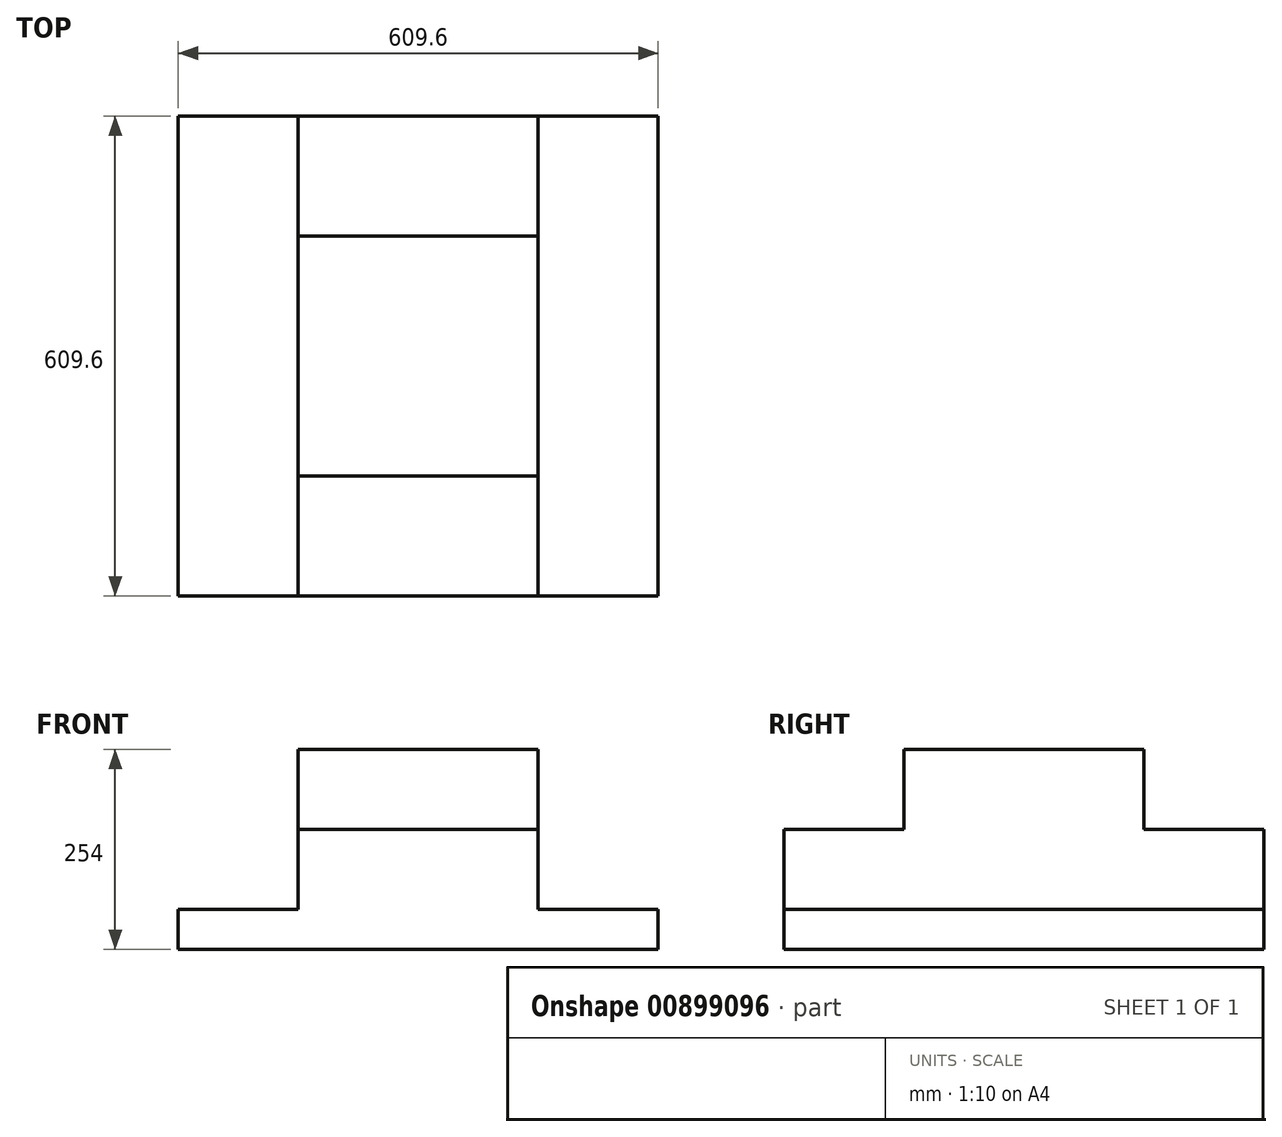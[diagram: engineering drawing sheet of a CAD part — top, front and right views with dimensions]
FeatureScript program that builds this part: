
annotation { "Feature Type Name" : "Feature", "Feature Type Description" : "" }
export const myFeature = defineFeature(function(context is Context, id is Id, definition is map)
    precondition{}
    {
        {
            var Q0;
            Q0=qCreatedBy(makeId("Top.planeOp"),FACE);
            var sketch = newSketch(context, id + "F0", { "sketchPlane" : qUnion([Q0])});
            skLineSegment(sketch, "E0.bottom", {"start": v(-152.4, 304.8) * mm, "end": v(152.4, 304.8) * mm});
            skLineSegment(sketch, "E0.top", {"start": v(-152.4, -304.8) * mm, "end": v(152.4, -304.8) * mm});
            skLineSegment(sketch, "E0.left", {"start": v(-152.4, 304.8) * mm, "end": v(-152.4, -304.8) * mm});
            skLineSegment(sketch, "E0.right", {"start": v(152.4, 304.8) * mm, "end": v(152.4, -304.8) * mm});
            skSolve(sketch);
        }
        {
            var Q0;
            Q0=makeQuery(id+"F0.imprint","IMPRINT",FACE,{"disambiguationData":[TD([[makeQuery(id+"F0.imprint","IMPRINT",EDGE,{"derivedFrom":sQuery(id+"F0.wireOp",EDGE,"E0.bottom")}),-1.0]])]});
            extrude(context, id + "F1", {"entities" : qUnion([Q0]), "depth" : 101.6 * mm, "offsetDistance" : 25.4 * mm});
        }
        {
            var Q0;
            Q0=qCreatedBy(makeId("Top.planeOp"),FACE);
            var sketch = newSketch(context, id + "F2", { "sketchPlane" : qUnion([Q0])});
            skLineSegment(sketch, "E1.bottom", {"start": v(-304.8, 304.8) * mm, "end": v(304.8, 304.8) * mm});
            skLineSegment(sketch, "E1.top", {"start": v(-304.8, -304.8) * mm, "end": v(304.8, -304.8) * mm});
            skLineSegment(sketch, "E1.left", {"start": v(-304.8, 304.8) * mm, "end": v(-304.8, -304.8) * mm});
            skLineSegment(sketch, "E1.right", {"start": v(304.8, 304.8) * mm, "end": v(304.8, -304.8) * mm});
            skSolve(sketch);
        }
        {
            var Q0;
            Q0=makeQuery(id+"F2.imprint","IMPRINT",FACE,{"disambiguationData":[TD([[makeQuery(id+"F2.imprint","IMPRINT",EDGE,{"derivedFrom":sQuery(id+"F2.wireOp",EDGE,"E1.bottom")}),-1.0]])]});
            extrude(context, id + "F3", {"entities" : qUnion([Q0]), "operationType" : NewBodyOperationType.ADD, "oppositeDirection" : true, "depth" : 50.8 * mm, "offsetDistance" : 25.4 * mm});
        }
        {
            var Q0;
            Q0=makeQuery(id+"F1.opExtrude","CAP_FACE",FACE,{"disambiguationData":[OSD([sQuery(id+"F0.wireOp",EDGE,"E0.bottom"),sQuery(id+"F0.wireOp",EDGE,"E0.top"),sQuery(id+"F0.wireOp",EDGE,"E0.left"),sQuery(id+"F0.wireOp",EDGE,"E0.right")])],"isStart":false});
            var sketch = newSketch(context, id + "F4", { "sketchPlane" : qUnion([Q0])});
            skLineSegment(sketch, "E2.bottom", {"start": v(-152.4, 152.4) * mm, "end": v(152.4, 152.4) * mm});
            skLineSegment(sketch, "E2.top", {"start": v(-152.4, -152.4) * mm, "end": v(152.4, -152.4) * mm});
            skLineSegment(sketch, "E2.left", {"start": v(-152.4, 152.4) * mm, "end": v(-152.4, -152.4) * mm});
            skLineSegment(sketch, "E2.right", {"start": v(152.4, 152.4) * mm, "end": v(152.4, -152.4) * mm});
            skSolve(sketch);
        }
        {
            var Q0;
            Q0=makeQuery(id+"F4.imprint","IMPRINT",FACE,{"disambiguationData":[TD([[makeQuery(id+"F4.imprint","IMPRINT",EDGE,{"derivedFrom":sQuery(id+"F4.wireOp",EDGE,"E2.bottom")}),-1.0]])]});
            extrude(context, id + "F5", {"entities" : qUnion([Q0]), "operationType" : NewBodyOperationType.ADD, "depth" : 101.6 * mm, "offsetDistance" : 25.4 * mm});
        }
    });
